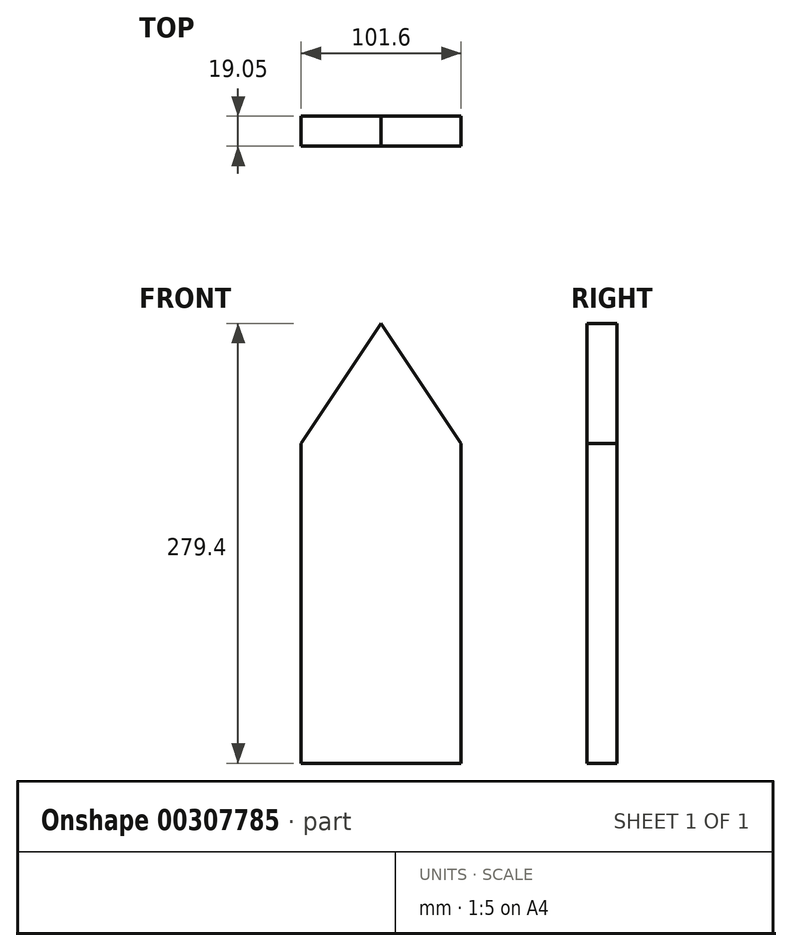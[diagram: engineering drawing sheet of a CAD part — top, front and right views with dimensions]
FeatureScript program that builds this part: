
annotation { "Feature Type Name" : "Feature", "Feature Type Description" : "" }
export const myFeature = defineFeature(function(context is Context, id is Id, definition is map)
    precondition{}
    {
        {
            var Q0;
            Q0=qCreatedBy(makeId("Front.planeOp"),FACE);
            var sketch = newSketch(context, id + "F0", { "sketchPlane" : qUnion([Q0])});
            skLineSegment(sketch, "E0.bottom", {"start": v(-50.8, 139.7) * mm, "end": v(50.8, 139.7) * mm});
            skLineSegment(sketch, "E0.top", {"start": v(-50.8, -139.7) * mm, "end": v(50.8, -139.7) * mm});
            skLineSegment(sketch, "E0.left", {"start": v(-50.8, 139.7) * mm, "end": v(-50.8, -139.7) * mm});
            skLineSegment(sketch, "E0.right", {"start": v(50.8, 139.7) * mm, "end": v(50.8, -139.7) * mm});
            skPoint(sketch, "E0.middle", {"position": v(0, 0) * mm});
            skLineSegment(sketch, "E1", {"start": v(50.8, 63.5) * mm, "end": v(0, 139.7) * mm});
            skLineSegment(sketch, "E2", {"start": v(-50.8, 63.5) * mm, "end": v(0, 139.7) * mm});
            skSolve(sketch);
        }
        {
            var Q0;
            {var subQ1=sQuery(id+"F0.wireOp",EDGE,"E0.top");Q0=makeQuery(id+"F0.imprint","IMPRINT",FACE,{"disambiguationData":[TD([[makeQuery(id+"F0.imprint","IMPRINT",EDGE,{"derivedFrom":subQ1}),1.0]])]});}
            extrude(context, id + "F1", {"entities" : qUnion([Q0]), "depth" : 19.05 * mm});
        }
    });
